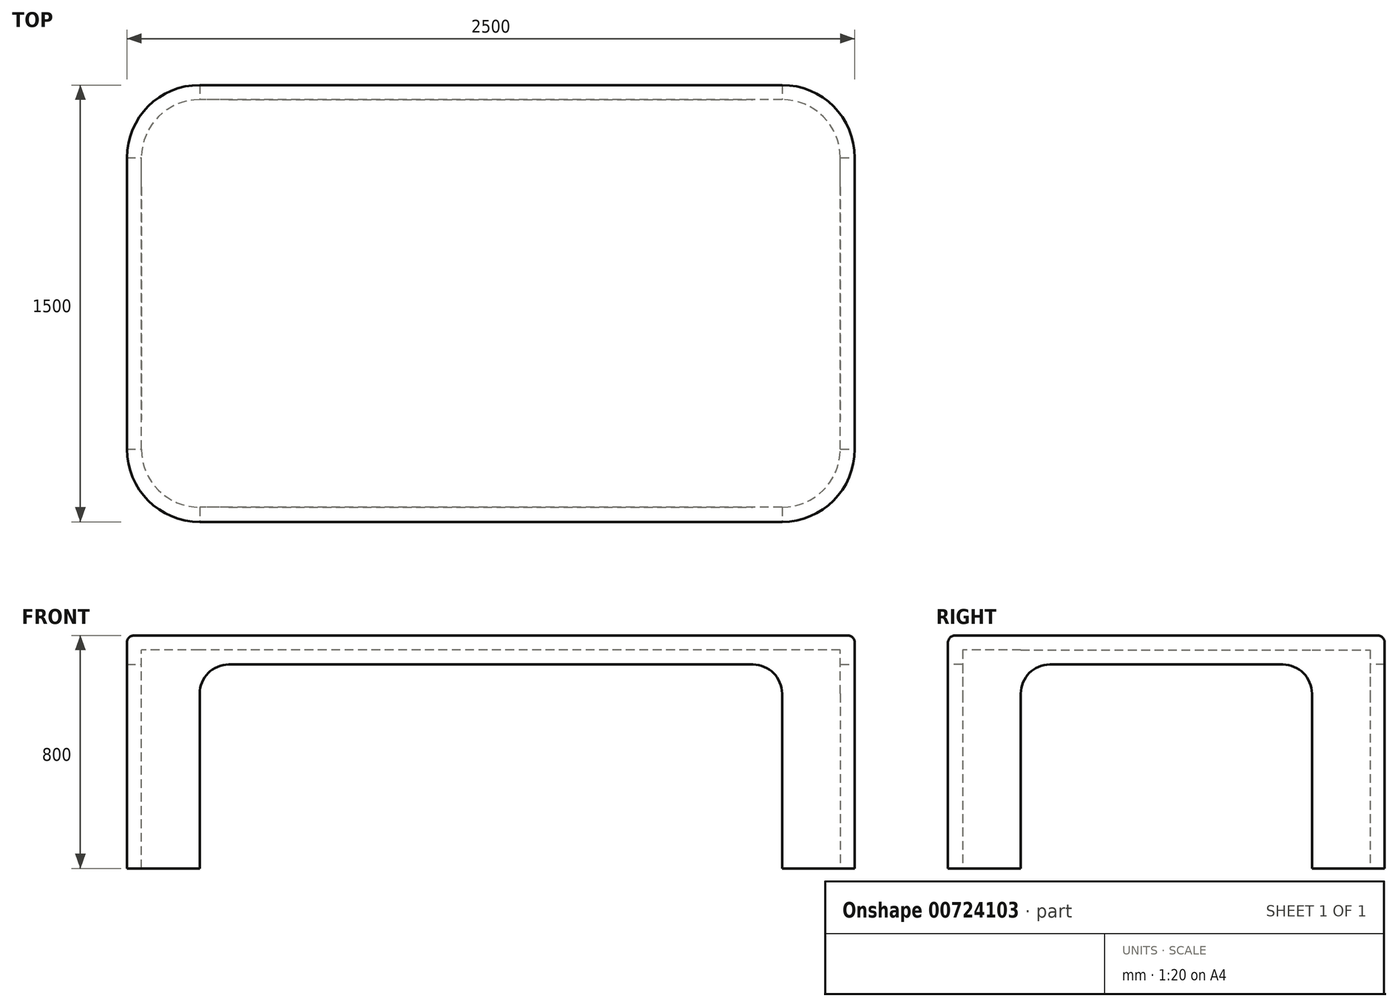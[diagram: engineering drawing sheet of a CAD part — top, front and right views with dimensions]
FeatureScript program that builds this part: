
annotation { "Feature Type Name" : "Feature", "Feature Type Description" : "" }
export const myFeature = defineFeature(function(context is Context, id is Id, definition is map)
    precondition{}
    {
        {
            var Q0;
            Q0=qCreatedBy(makeId("Top.planeOp"),FACE);
            var sketch = newSketch(context, id + "F0", { "sketchPlane" : qUnion([Q0])});
            skLineSegment(sketch, "E0.bottom", {"start": v(1000, -750) * mm, "end": v(-1000, -750) * mm});
            skLineSegment(sketch, "E0.top", {"start": v(1000, 750) * mm, "end": v(-1000, 750) * mm});
            skLineSegment(sketch, "E0.left", {"start": v(1250, -500) * mm, "end": v(1250, 500) * mm});
            skLineSegment(sketch, "E0.right", {"start": v(-1250, -500) * mm, "end": v(-1250, 500) * mm});
            skPoint(sketch, "E0.middle", {"position": v(0, 0) * mm});
            skPoint(sketch, "E1.visualSharp", {"position": v(-1250, 750) * mm});
            skArc(sketch, "E1.filletArc", {"start": v(-1000, 750) * mm, "mid": v(-1176.78, 676.78) * mm, "end": v(-1250, 500) * mm});
            skPoint(sketch, "E2.visualSharp", {"position": v(1250, 750) * mm});
            skArc(sketch, "E2.filletArc", {"start": v(1250, 500) * mm, "mid": v(1176.78, 676.78) * mm, "end": v(1000, 750) * mm});
            skPoint(sketch, "E3.visualSharp", {"position": v(1250, -750) * mm});
            skArc(sketch, "E3.filletArc", {"start": v(1000, -750) * mm, "mid": v(1176.78, -676.78) * mm, "end": v(1250, -500) * mm});
            skPoint(sketch, "E4.visualSharp", {"position": v(-1250, -750) * mm});
            skArc(sketch, "E4.filletArc", {"start": v(-1250, -500) * mm, "mid": v(-1176.78, -676.78) * mm, "end": v(-1000, -750) * mm});
            skCircle(sketch, "E5", {"center": v(-1000, -500) * mm, "radius": 50 * mm});
            skCircle(sketch, "E6", {"center": v(1000, -500) * mm, "radius": 50 * mm});
            skCircle(sketch, "E7", {"center": v(1000, 500) * mm, "radius": 50 * mm});
            skCircle(sketch, "E8", {"center": v(-1000, 500) * mm, "radius": 50 * mm});
            skSolve(sketch);
        }
        {
            var Q0;
            Q0 = qSketchRegion(id + "F0", true);
            var Q1;
            Q1=makeQuery(id+"F0.imprint","IMPRINT",FACE,{"disambiguationData":[TD([[makeQuery(id+"F0.imprint","IMPRINT",EDGE,{"derivedFrom":sQuery(id+"F0.wireOp",EDGE,"E5")}),1.0]])]});
            var Q2;
            Q2=makeQuery(id+"F0.imprint","IMPRINT",FACE,{"disambiguationData":[TD([[makeQuery(id+"F0.imprint","IMPRINT",EDGE,{"derivedFrom":sQuery(id+"F0.wireOp",EDGE,"E6")}),1.0]])]});
            var Q3;
            Q3=makeQuery(id+"F0.imprint","IMPRINT",FACE,{"disambiguationData":[TD([[makeQuery(id+"F0.imprint","IMPRINT",EDGE,{"derivedFrom":sQuery(id+"F0.wireOp",EDGE,"E7")}),1.0]])]});
            var Q4;
            Q4=makeQuery(id+"F0.imprint","IMPRINT",FACE,{"disambiguationData":[TD([[makeQuery(id+"F0.imprint","IMPRINT",EDGE,{"derivedFrom":sQuery(id+"F0.wireOp",EDGE,"E8")}),1.0]])]});
            extrude(context, id + "F1", {"entities" : qUnion([Q0, Q1, Q2, Q3, Q4]), "depth" : 800 * mm, "offsetDistance" : 25 * mm});
        }
        {
            var Q0;
            Q0=makeQuery(id+"F1.opExtrude","CAP_FACE",FACE,{"disambiguationData":[OSD([sQuery(id+"F0.wireOp",EDGE,"E0.bottom"),sQuery(id+"F0.wireOp",EDGE,"E0.top"),sQuery(id+"F0.wireOp",EDGE,"E0.left"),sQuery(id+"F0.wireOp",EDGE,"E0.right"),sQuery(id+"F0.wireOp",EDGE,"E1.filletArc"),sQuery(id+"F0.wireOp",EDGE,"E2.filletArc"),sQuery(id+"F0.wireOp",EDGE,"E3.filletArc"),sQuery(id+"F0.wireOp",EDGE,"E4.filletArc")])],"isStart":true});
            shell(context, id + "F2", {"entities" : qUnion([Q0]), "thickness" : 50 * mm});
        }
        {
            var Q0;
            Q0=makeQuery(id+"F1.opExtrude","SWEPT_FACE",FACE,{"disambiguationData":[OSD([sQuery(id+"F0.wireOp",EDGE,"E0.bottom")])]});
            var sketch = newSketch(context, id + "F3", { "sketchPlane" : qUnion([Q0])});
            skLineSegment(sketch, "E9.bottom", {"start": v(-1000, 0) * mm, "end": v(1000, 0) * mm});
            skLineSegment(sketch, "E9.top", {"start": v(-900, 700) * mm, "end": v(900, 700) * mm});
            skLineSegment(sketch, "E9.left", {"start": v(-1000, 0) * mm, "end": v(-1000, 600) * mm});
            skLineSegment(sketch, "E9.right", {"start": v(1000, 0) * mm, "end": v(1000, 600) * mm});
            skPoint(sketch, "E10.visualSharp", {"position": v(-1000, 700) * mm});
            skArc(sketch, "E10.filletArc", {"start": v(-900, 700) * mm, "mid": v(-970.71, 670.71) * mm, "end": v(-1000, 600) * mm});
            skPoint(sketch, "E11.visualSharp", {"position": v(1000, 700) * mm});
            skArc(sketch, "E11.filletArc", {"start": v(1000, 600) * mm, "mid": v(970.71, 670.71) * mm, "end": v(900, 700) * mm});
            skSolve(sketch);
        }
        {
            var Q0;
            Q0=makeQuery(id+"F3.imprint","IMPRINT",FACE,{"disambiguationData":[TD([[makeQuery(id+"F3.imprint","IMPRINT",EDGE,{"derivedFrom":sQuery(id+"F3.wireOp",EDGE,"E9.bottom")}),-1.0]])]});
            extrude(context, id + "F4", {"entities" : qUnion([Q0]), "operationType" : NewBodyOperationType.REMOVE, "endBound" : BoundingType.THROUGH_ALL, "oppositeDirection" : true, "depth" : 25 * mm, "offsetDistance" : 25 * mm});
        }
        {
            var Q0;
            Q0=makeQuery(id+"F1.opExtrude","SWEPT_FACE",FACE,{"disambiguationData":[OSD([sQuery(id+"F0.wireOp",EDGE,"E0.left")])]});
            var sketch = newSketch(context, id + "F5", { "sketchPlane" : qUnion([Q0])});
            skLineSegment(sketch, "E12.bottom", {"start": v(-500, 0) * mm, "end": v(500, 0) * mm});
            skLineSegment(sketch, "E12.top", {"start": v(-400, 700) * mm, "end": v(400, 700) * mm});
            skLineSegment(sketch, "E12.left", {"start": v(-500, 0) * mm, "end": v(-500, 600) * mm});
            skLineSegment(sketch, "E12.right", {"start": v(500, 0) * mm, "end": v(500, 600) * mm});
            skPoint(sketch, "E13.visualSharp", {"position": v(-500, 700) * mm});
            skArc(sketch, "E13.filletArc", {"start": v(-400, 700) * mm, "mid": v(-470.71, 670.71) * mm, "end": v(-500, 600) * mm});
            skPoint(sketch, "E14.visualSharp", {"position": v(500, 700) * mm});
            skArc(sketch, "E14.filletArc", {"start": v(500, 600) * mm, "mid": v(470.71, 670.71) * mm, "end": v(400, 700) * mm});
            skSolve(sketch);
        }
        {
            var Q0;
            Q0=makeQuery(id+"F5.imprint","IMPRINT",FACE,{"disambiguationData":[TD([[makeQuery(id+"F5.imprint","IMPRINT",EDGE,{"derivedFrom":sQuery(id+"F5.wireOp",EDGE,"E12.bottom")}),1.0]])]});
            extrude(context, id + "F6", {"entities" : qUnion([Q0]), "operationType" : NewBodyOperationType.REMOVE, "endBound" : BoundingType.THROUGH_ALL, "oppositeDirection" : true, "depth" : 25 * mm, "offsetDistance" : 25 * mm});
        }
        {
            var Q0;
            Q0=makeQuery(id+"F1.opExtrude","CAP_FACE",FACE,{"disambiguationData":[OSD([sQuery(id+"F0.wireOp",EDGE,"E0.bottom"),sQuery(id+"F0.wireOp",EDGE,"E0.top"),sQuery(id+"F0.wireOp",EDGE,"E0.left"),sQuery(id+"F0.wireOp",EDGE,"E0.right"),sQuery(id+"F0.wireOp",EDGE,"E1.filletArc"),sQuery(id+"F0.wireOp",EDGE,"E2.filletArc"),sQuery(id+"F0.wireOp",EDGE,"E3.filletArc"),sQuery(id+"F0.wireOp",EDGE,"E4.filletArc")])],"isStart":false});
            fillet(context, id + "F7", {"entities" : qUnion([Q0]), "radius" : 25 * mm, "tangentPropagation" : true, "allowEdgeOverflow" : false});
        }
    });
